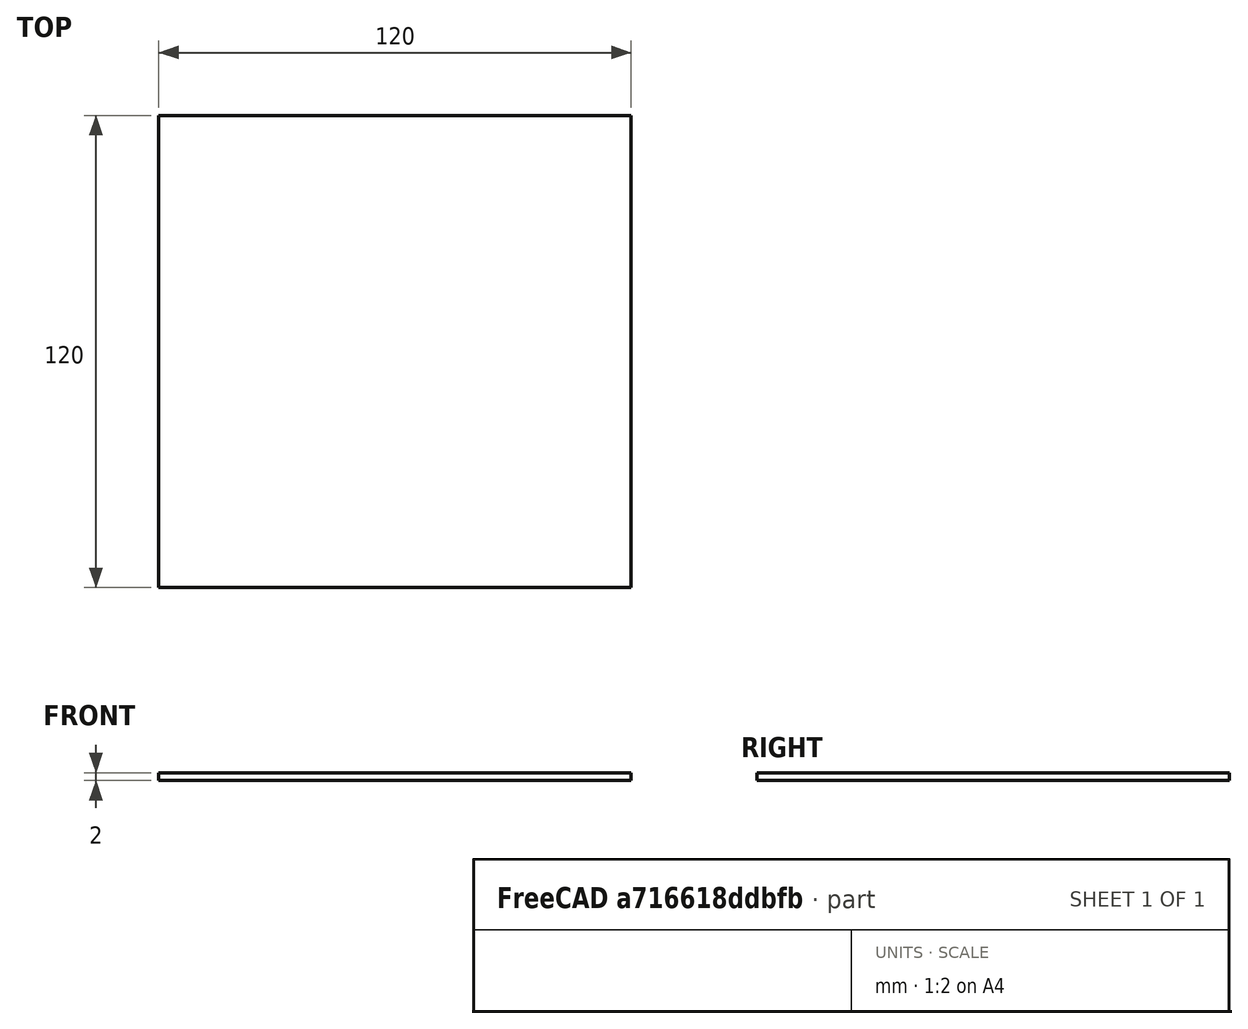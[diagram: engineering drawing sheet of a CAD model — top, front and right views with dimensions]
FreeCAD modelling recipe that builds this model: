
FCSTD DOCUMENT  (FreeCAD 0.19R24276 (Git))
Label: GroundPlate
License: All rights reserved
LicenseURL: http://en.wikipedia.org/wiki/All_rights_reserved
objects: Sketcher::SketchObject×1, PartDesign::Pad×1, PartDesign::Body×1, App::Part×1
note: 4 computed .brp shape members not serialized (recipe doc carries the construction recipe); baked Part::Feature solids carry a one-line shape summary decoded from their .brp

FEATURE [Sketcher::SketchObject] Sketch
  FullyConstrained = true
  MapMode = 5
  Support = -> [XY_Plane001]
  sketch-geometry (4):
    g0: LineSegment StartX=-60 StartY=60 StartZ=0 EndX=60 EndY=60 EndZ=0
    g1: LineSegment StartX=60 StartY=60 StartZ=0 EndX=60 EndY=-60 EndZ=0
    g2: LineSegment StartX=60 StartY=-60 StartZ=0 EndX=-60 EndY=-60 EndZ=0
    g3: LineSegment StartX=-60 StartY=-60 StartZ=0 EndX=-60 EndY=60 EndZ=0
  constraints (11):
    c: Coincident(g0,g1)
    c: Coincident(g1,g2)
    c: Coincident(g2,g3)
    c: Coincident(g3,g0)
    c: Horizontal(g0)
    c: Horizontal(g2)
    c: Vertical(g1)
    c: Vertical(g3)
    c: Symmetric(g0,g2,g-1)
    c: Distance(g0) = 120
    c: Distance(g1) = 120
FEATURE [PartDesign::Pad] Pad
  Direction = (1,1,1)
  Length = 2
  Length2 = 100
  Profile = -> Sketch
  Reversed = true
  Type = 0
FEATURE [PartDesign::Body] Body  label="Plate"
  Group = -> [Sketch,Pad]
  Origin = -> Origin001
  Tip = -> Pad
FEATURE [App::Part] Part  label="Ground"
  Group = -> [Body]
  Origin = -> Origin
